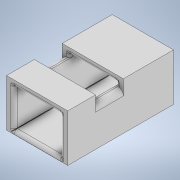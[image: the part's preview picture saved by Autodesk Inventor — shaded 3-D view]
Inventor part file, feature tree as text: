
AUTODESK INVENTOR PART (.ipt)
format: ipt  version: 2020 (Build 240168000, 168)  size: 347,648 bytes
history: native  units: in
note: dims shown in document units (in); Inventor stores cm internally (conversion verified against a paired STEP export)
features: extrude x11, sketch x11, projected_geometry x11, fillet x4
ambient origin geometry x8: Origin, YZ Plane, XZ Plane, XY Plane, X Axis, Y Axis, Z Axis, Center Point
bodies: Solid1 (feature_tree)
feature tree (37):
  extrude  "Extrusion1"  Depth=3.7402in
  extrude  "Extrusion2"  Depth=0.0984in
  extrude  "Extrusion3"  Depth=1.378in
  extrude  "Extrusion4"  Depth=1.7717in
  extrude  "Extrusion5"  Depth=0.2362in TaperAngle=0.0deg
  extrude  "Extrusion6"  Depth=0.2362in TaperAngle=0.0deg
  extrude  "Extrusion7"  Depth=0.0984in TaperAngle=0.0deg
  extrude  "Extrusion9"  Depth=0.0197in
  extrude  "Extrusion11"  Depth=0.8268in
  extrude  "Extrusion12"  Depth=0.6644in
  extrude  "Extrusion15"  TaperAngle=180.0deg  [1 undecoded]
  fillet  "Fillet1"  Radius=0.0197in
  fillet  "Fillet2"  Radius=0.0197in
  fillet  "Fillet3"  Radius=0.1181in
  fillet  "Fillet4"  Radius=0.0197in
  sketch  "Sketch1"  dims[d0=1.9685in d1=3.7402in]
  sketch  "Sketch2"  dims[d2=1.5748in d3=0.0in d4=0.0984in]
  projected_geometry  "Projected Loop1"
  sketch  "Sketch3"  dims[d5=1.7717in d6=1.378in]
  projected_geometry  "Projected Loop2"
  sketch  "Sketch4"  dims[d7=3.5433in d8=0.0in d9=1.7717in]
  projected_geometry  "Projected Loop3"
  sketch  "Sketch5"  dims[d10=2.7559in d11=0.2362in d12=0.0in]
  projected_geometry  "Projected Loop4"
  sketch  "Sketch6"  dims[d13=0.9843in d14=0.2362in d15=0.0in]
  projected_geometry  "Projected Loop5"
  sketch  "Sketch7"  dims[d16=0.0984in d17=0.0in d18=0.0984in d19=0.0in]
  projected_geometry  "Projected Loop6"
  projected_geometry  "Projected Loop7"
  sketch  "Sketch10"  dims[d20=0.0984in d21=0.0in d29=0.0197in]
  projected_geometry  "Projected Loop9"
  sketch  "Sketch11"  dims[d30=0.0984in d31=0.0in d49=0.8268in]
  projected_geometry  "Projected Loop10"
  sketch  "Sketch12"  dims[d50=0.8268in d51=0.6644in]
  projected_geometry  "Projected Loop11"
  sketch  "Sketch16"  dims[d52=0.3937in d53=0.0in d54=180.0deg d55=0.0197in d56=0.0197in d58=0.1181in d59=0.0197in d60=0.3937in d61=0.0in d66=0.3937in d67=0.0in d68=0.1969in d69=0.1181in d70=0.1181in d71=0.1181in]
  projected_geometry  "Projected Loop15"
note: 1 required parameter value undecoded (feature->parameter linkage not recoverable at this tier; creation-order binding heuristic only, values carry confidence <= 0.55)
